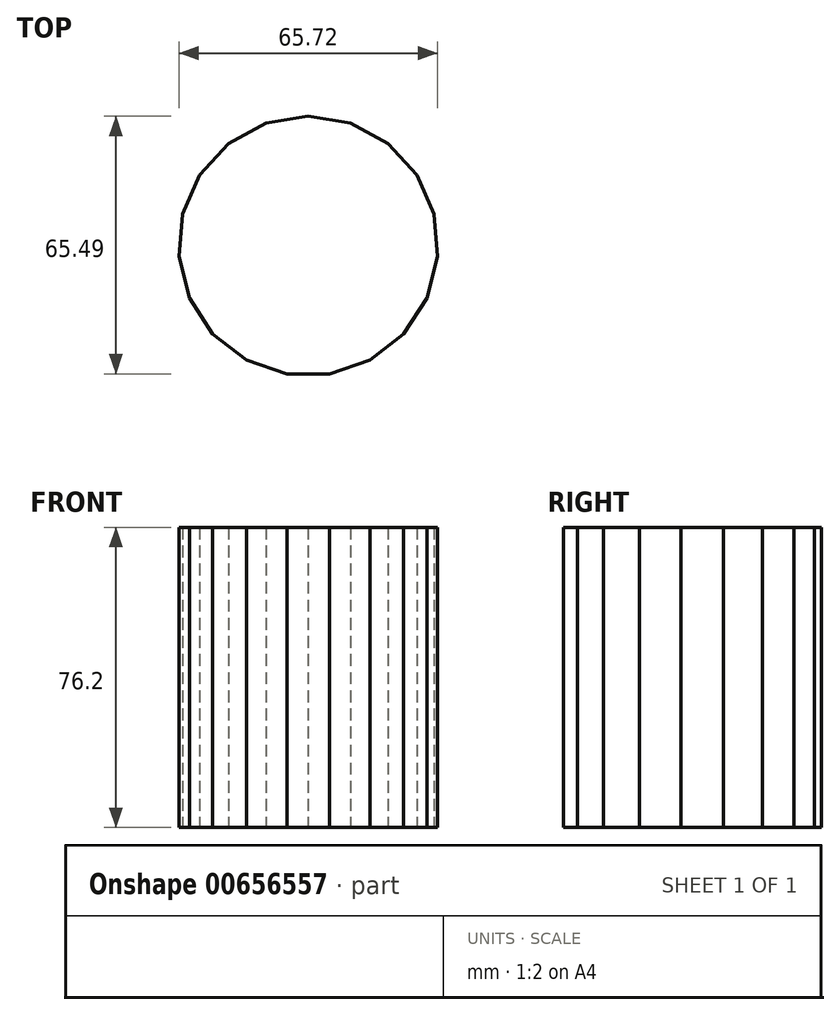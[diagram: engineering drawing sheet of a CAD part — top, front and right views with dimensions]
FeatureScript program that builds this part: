
annotation { "Feature Type Name" : "Feature", "Feature Type Description" : "" }
export const myFeature = defineFeature(function(context is Context, id is Id, definition is map)
    precondition{}
    {
        {
            var Q0;
            Q0=qCreatedBy(makeId("Top.planeOp"),FACE);
            var sketch = newSketch(context, id + "F0", { "sketchPlane" : qUnion([Q0])});
            skCircle(sketch, "E0.cCircle", {"center": v(0, 17.32) * mm, "radius": 32.52 * mm, "construction": true});
            skLineSegment(sketch, "E0.0", {"start": v(5.43, -15.2) * mm, "end": v(-5.43, -15.2) * mm});
            skLineSegment(sketch, "E0.1", {"start": v(-5.43, -15.2) * mm, "end": v(-15.7, -11.68) * mm});
            skLineSegment(sketch, "E0.2", {"start": v(-15.7, -11.68) * mm, "end": v(-24.26, -5.01) * mm});
            skLineSegment(sketch, "E0.3", {"start": v(-24.26, -5.01) * mm, "end": v(-30.2, 4.07) * mm});
            skLineSegment(sketch, "E0.4", {"start": v(-30.2, 4.07) * mm, "end": v(-32.86, 14.6) * mm});
            skLineSegment(sketch, "E0.5", {"start": v(-32.86, 14.6) * mm, "end": v(-31.96, 25.41) * mm});
            skLineSegment(sketch, "E0.6", {"start": v(-31.96, 25.41) * mm, "end": v(-27.6, 35.35) * mm});
            skLineSegment(sketch, "E0.7", {"start": v(-27.6, 35.35) * mm, "end": v(-20.25, 43.34) * mm});
            skLineSegment(sketch, "E0.8", {"start": v(-20.25, 43.34) * mm, "end": v(-10.7, 48.5) * mm});
            skLineSegment(sketch, "E0.9", {"start": v(-10.7, 48.5) * mm, "end": v(0, 50.29) * mm});
            skLineSegment(sketch, "E0.10", {"start": v(0, 50.29) * mm, "end": v(10.7, 48.5) * mm});
            skLineSegment(sketch, "E0.11", {"start": v(10.7, 48.5) * mm, "end": v(20.25, 43.34) * mm});
            skLineSegment(sketch, "E0.12", {"start": v(20.25, 43.34) * mm, "end": v(27.6, 35.35) * mm});
            skLineSegment(sketch, "E0.13", {"start": v(27.6, 35.35) * mm, "end": v(31.96, 25.41) * mm});
            skLineSegment(sketch, "E0.14", {"start": v(31.96, 25.41) * mm, "end": v(32.86, 14.6) * mm});
            skLineSegment(sketch, "E0.15", {"start": v(32.86, 14.6) * mm, "end": v(30.2, 4.07) * mm});
            skLineSegment(sketch, "E0.16", {"start": v(30.2, 4.07) * mm, "end": v(24.26, -5.01) * mm});
            skLineSegment(sketch, "E0.17", {"start": v(24.26, -5.01) * mm, "end": v(15.7, -11.68) * mm});
            skLineSegment(sketch, "E0.18", {"start": v(15.7, -11.68) * mm, "end": v(5.43, -15.2) * mm});
            skPoint(sketch, "E0.0.midPoint", {"position": v(0, -15.2) * mm});
            skSolve(sketch);
        }
        {
            var Q0;
            Q0 = qSketchRegion(id + "F0", true);
            extrude(context, id + "F1", {"entities" : qUnion([Q0]), "depth" : 76.2 * mm, "offsetDistance" : 25.4 * mm});
        }
    });
